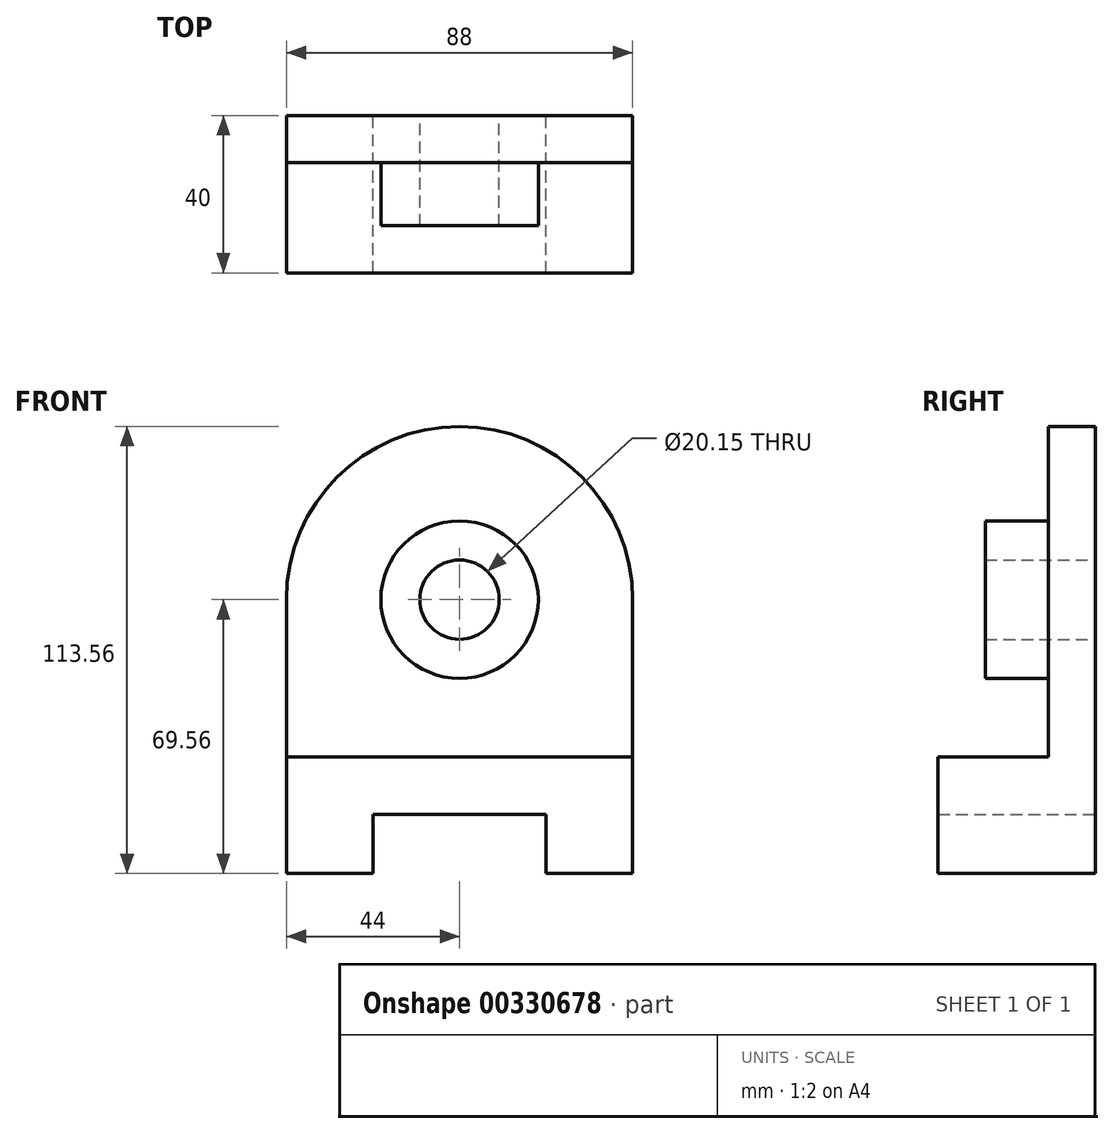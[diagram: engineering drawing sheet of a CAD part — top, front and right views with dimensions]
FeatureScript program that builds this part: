
annotation { "Feature Type Name" : "Feature", "Feature Type Description" : "" }
export const myFeature = defineFeature(function(context is Context, id is Id, definition is map)
    precondition{}
    {
        {
            var Q0;
            Q0=qCreatedBy(makeId("Front.planeOp"),FACE);
            var sketch = newSketch(context, id + "F0", { "sketchPlane" : qUnion([Q0])});
            skLineSegment(sketch, "E0", {"start": v(-44, 0) * mm, "end": v(44, 0) * mm});
            skLineSegment(sketch, "E1", {"start": v(44, 0) * mm, "end": v(44, 40) * mm});
            skLineSegment(sketch, "E2", {"start": v(-44, 0) * mm, "end": v(-44, 40) * mm});
            skArc(sketch, "E3", {"start": v(44, 40) * mm, "mid": v(0, 84) * mm, "end": v(-44, 40) * mm});
            skSolve(sketch);
        }
        {
            var Q0;
            Q0 = qSketchRegion(id + "F0", true);
            extrude(context, id + "F1", {"entities" : qUnion([Q0]), "depth" : 12 * mm});
        }
        {
            var Q0;
            Q0=qCreatedBy(makeId("Front.planeOp"),FACE);
            var sketch = newSketch(context, id + "F2", { "sketchPlane" : qUnion([Q0])});
            skLineSegment(sketch, "E4", {"start": v(-44, 0) * mm, "end": v(-44, -29.56) * mm});
            skLineSegment(sketch, "E5", {"start": v(-44, -29.56) * mm, "end": v(-22, -29.56) * mm});
            skLineSegment(sketch, "E6", {"start": v(-22, -29.56) * mm, "end": v(-22, -14.56) * mm});
            skLineSegment(sketch, "E7", {"start": v(-22, -14.56) * mm, "end": v(22, -14.56) * mm});
            skLineSegment(sketch, "E8", {"start": v(22, -14.56) * mm, "end": v(22, -29.56) * mm});
            skLineSegment(sketch, "E9", {"start": v(22, -29.56) * mm, "end": v(44, -29.56) * mm});
            skLineSegment(sketch, "E10", {"start": v(44, -29.56) * mm, "end": v(44, 0) * mm});
            skLineSegment(sketch, "E11", {"start": v(44, 0) * mm, "end": v(-44, 0) * mm});
            skSolve(sketch);
        }
        {
            var Q0;
            Q0 = qSketchRegion(id + "F2", true);
            extrude(context, id + "F3", {"entities" : qUnion([Q0]), "operationType" : NewBodyOperationType.ADD, "depth" : 40 * mm});
        }
        {
            var Q0;
            Q0=qCreatedBy(makeId("Front.planeOp"),FACE);
            var sketch = newSketch(context, id + "F4", { "sketchPlane" : qUnion([Q0])});
            skLineSegment(sketch, "E12", {"start": v(0, 0) * mm, "end": v(-44, 0) * mm, "construction": true});
            skLineSegment(sketch, "E13", {"start": v(-44, 0) * mm, "end": v(-44, 40) * mm, "construction": true});
            skLineSegment(sketch, "E14", {"start": v(-44, 40) * mm, "end": v(44, 40) * mm, "construction": true});
            skLineSegment(sketch, "E15", {"start": v(44, 40) * mm, "end": v(44, 0) * mm, "construction": true});
            skLineSegment(sketch, "E16", {"start": v(44, 0) * mm, "end": v(0, 0) * mm, "construction": true});
            skLineSegment(sketch, "E17", {"start": v(0, 0) * mm, "end": v(0, 40) * mm, "construction": true});
            skLineSegment(sketch, "E18", {"start": v(-44, 20) * mm, "end": v(44, 20) * mm, "construction": true});
            skCircle(sketch, "E19", {"center": v(0, 40) * mm, "radius": 20 * mm});
            skCircle(sketch, "E20", {"center": v(0, 40) * mm, "radius": 10.08 * mm});
            skSolve(sketch);
        }
        {
            var Q0;
            Q0 = qSketchRegion(id + "F4", true);
            extrude(context, id + "F5", {"entities" : qUnion([Q0]), "operationType" : NewBodyOperationType.ADD, "depth" : 28 * mm});
        }
        {
            var Q0;
            Q0=makeQuery(id+"F5.boolean.opBoolean","SPLIT",FACE,{"disambiguationData":[TD([makeQuery(id+"F5.opExtrude","SWEPT_FACE",FACE,{"disambiguationData":[OSD([sQuery(id+"F4.wireOp",EDGE,"E20")])]})])],"derivedFrom":makeQuery(id+"F1.opExtrude","CAP_FACE",FACE,{"disambiguationData":[OSD([sQuery(id+"F0.wireOp",EDGE,"E0"),sQuery(id+"F0.wireOp",EDGE,"E1"),sQuery(id+"F0.wireOp",EDGE,"E2"),sQuery(id+"F0.wireOp",EDGE,"E3")])],"isStart":false})});
            extrude(context, id + "F6", {"entities" : qUnion([Q0]), "operationType" : NewBodyOperationType.REMOVE, "oppositeDirection" : true, "depth" : 25 * mm});
        }
    });
